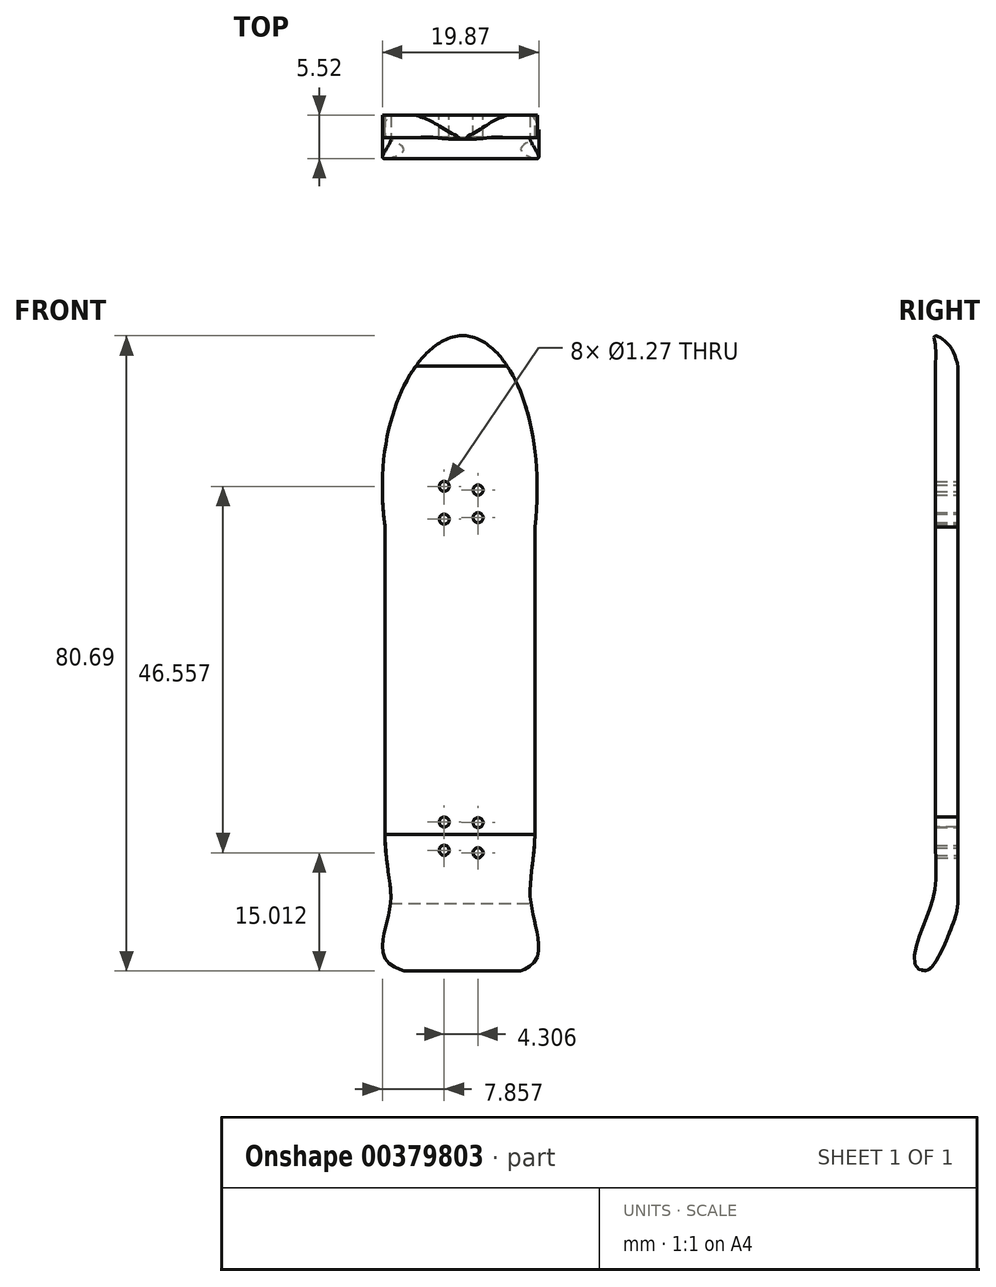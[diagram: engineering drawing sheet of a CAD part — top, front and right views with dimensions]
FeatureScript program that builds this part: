
annotation { "Feature Type Name" : "Feature", "Feature Type Description" : "" }
export const myFeature = defineFeature(function(context is Context, id is Id, definition is map)
    precondition{}
    {
        {
            var Q0;
            Q0=qCreatedBy(makeId("Front.planeOp"),FACE);
            var sketch = newSketch(context, id + "F0", { "sketchPlane" : qUnion([Q0])});
            skLineSegment(sketch, "E0", {"start": v(9.14, 0) * mm, "end": v(9.14, -36.87) * mm});
            skLineSegment(sketch, "E1.0", {"start": v(-9.9, 0) * mm, "end": v(-9.9, -38.1) * mm});
            skFitSpline(sketch, "E2", {"points": [v(9.14, 0) * mm, v(0, 24.3) * mm, v(-9.9, 0) * mm], "startDerivative": vector(9.42, 82.49) * mm, "endDerivative": vector(11.16, -82.8) * mm});
            skLineSegment(sketch, "E3", {"start": v(0, 0) * mm, "end": v(0, -36.13) * mm});
            skFitSpline(sketch, "E4", {"points": [v(-9.9, -38.1) * mm, v(-9.24, -48) * mm, v(-9.9, -54.83) * mm, v(0, -57.12) * mm, v(9.27, -54.97) * mm, v(8.6, -47.6) * mm, v(9.14, -36.87) * mm], "startDerivative": vector(-2.29, -81.95) * mm, "endDerivative": vector(-2.12, 90.84) * mm});
            skPoint(sketch, "E5", {"position": v(1.91, -37.57) * mm});
            skPoint(sketch, "E6", {"position": v(-2.4, -37.5) * mm});
            skPoint(sketch, "E7", {"position": v(-2.4, -41.08) * mm});
            skPoint(sketch, "E8", {"position": v(1.91, -41.4) * mm});
            skPoint(sketch, "E9", {"position": v(-2.4, 0.99) * mm});
            skPoint(sketch, "E10", {"position": v(1.91, 1.18) * mm});
            skPoint(sketch, "E11", {"position": v(1.91, 4.68) * mm});
            skPoint(sketch, "E12", {"position": v(-2.4, 5.16) * mm});
            skLineSegment(sketch, "E13", {"start": v(-9.9, -39.63) * mm, "end": v(9.1, -39.63) * mm});
            skPoint(sketch, "E13.startSnap0", {"position": v(-9.9, -19.05) * mm});
            skSolve(sketch);
        }
        {
            var Q0;
            {var subQ3=sQuery(id+"F0.wireOp",EDGE,"E0");Q0=makeQuery(id+"F0.imprint","IMPRINT",FACE,{"disambiguationData":[TD([[makeQuery(id+"F0.imprint","IMPRINT",EDGE,{"derivedFrom":subQ3}),-1.0]])]});}
            var Q1;
            {var subQ0=sQuery(id+"F0.wireOp",EDGE,"E13");Q1=makeQuery(id+"F0.imprint","IMPRINT",FACE,{"disambiguationData":[TD([[makeQuery(id+"F0.imprint","IMPRINT",EDGE,{"derivedFrom":subQ0}),-1.0]])]});}
            extrude(context, id + "F1", {"entities" : qUnion([Q0, Q1]), "depth" : 11.18 * mm});
        }
        {
            var Q0;
            Q0=qCreatedBy(makeId("Right.planeOp"),FACE);
            var sketch = newSketch(context, id + "F2", { "sketchPlane" : qUnion([Q0])});
            skLineSegment(sketch, "E14", {"start": v(-2.84, 20.44) * mm, "end": v(-2.84, -39.04) * mm});
            skLineSegment(sketch, "E15", {"start": v(0, -50.82) * mm, "end": v(0, 20.32) * mm});
            skFitSpline(sketch, "E16", {"points": [v(-2.84, -39.04) * mm, v(-2.84, -45.5) * mm, v(-4.34, -50.5) * mm, v(-5.52, -54.98) * mm, v(-4.92, -56.22) * mm, v(-3.5, -56.06) * mm, v(-0.54, -50.16) * mm, v(0, -47.85) * mm], "startDerivative": vector(-1.19, -24.8) * mm, "endDerivative": vector(3.4, 31.17) * mm});
            skFitSpline(sketch, "E17", {"points": [v(-2.84, 20.44) * mm, v(-2.84, 23.03) * mm, v(-2.92, 24.26) * mm, v(-0.95, 22.88) * mm, v(-0.15, 21) * mm, v(0, 20.32) * mm], "startDerivative": vector(0.14, 10.44) * mm, "endDerivative": vector(0, -8.8) * mm});
            skSolve(sketch);
        }
        {
            var Q0;
            Q0 = qSketchRegion(id + "F2", true);
            extrude(context, id + "F3", {"entities" : qUnion([Q0]), "operationType" : NewBodyOperationType.INTERSECT, "endBound" : BoundingType.SYMMETRIC, "oppositeDirection" : true, "depth" : 32 * mm});
        }
        {
            var Q0;
            Q0=sQuery(id+"F0.wireOp",VERTEX,"E8");
            var Q1;
            Q1=sQuery(id+"F0.wireOp",VERTEX,"E7");
            var Q2;
            Q2=sQuery(id+"F0.wireOp",VERTEX,"E6");
            var Q3;
            Q3=sQuery(id+"F0.wireOp",VERTEX,"E5");
            var Q4;
            Q4=sQuery(id+"F0.wireOp",VERTEX,"E10");
            var Q5;
            Q5=sQuery(id+"F0.wireOp",VERTEX,"E9");
            var Q6;
            Q6=sQuery(id+"F0.wireOp",VERTEX,"E12");
            var Q7;
            Q7=sQuery(id+"F0.wireOp",VERTEX,"E11");
            var Q8;
            Q8=makeQuery(id+"F1.opExtrude","SWEPT_BODY",BODY,{"disambiguationData":[OSD([sQuery(id+"F0.wireOp",EDGE,"E0"),sQuery(id+"F0.wireOp",EDGE,"E1.0"),sQuery(id+"F0.wireOp",EDGE,"E2"),sQuery(id+"F0.wireOp",EDGE,"E4")])]});
            hole(context, id + "F4", {"style" : HoleStyle.SIMPLE, "endStyle" : HoleEndStyle.BLIND, "oppositeDirection" : true, "holeDiameter" : 1.27 * mm, "holeDepth" : 12.7 * mm, "isTappedThrough" : true, "tappedDepth" : 12.7 * mm, "tapClearance" : 3, "locations" : qUnion([Q0, Q1, Q2, Q3, Q4, Q5, Q6, Q7]), "scope" : qUnion([Q8])});
        }
    });
